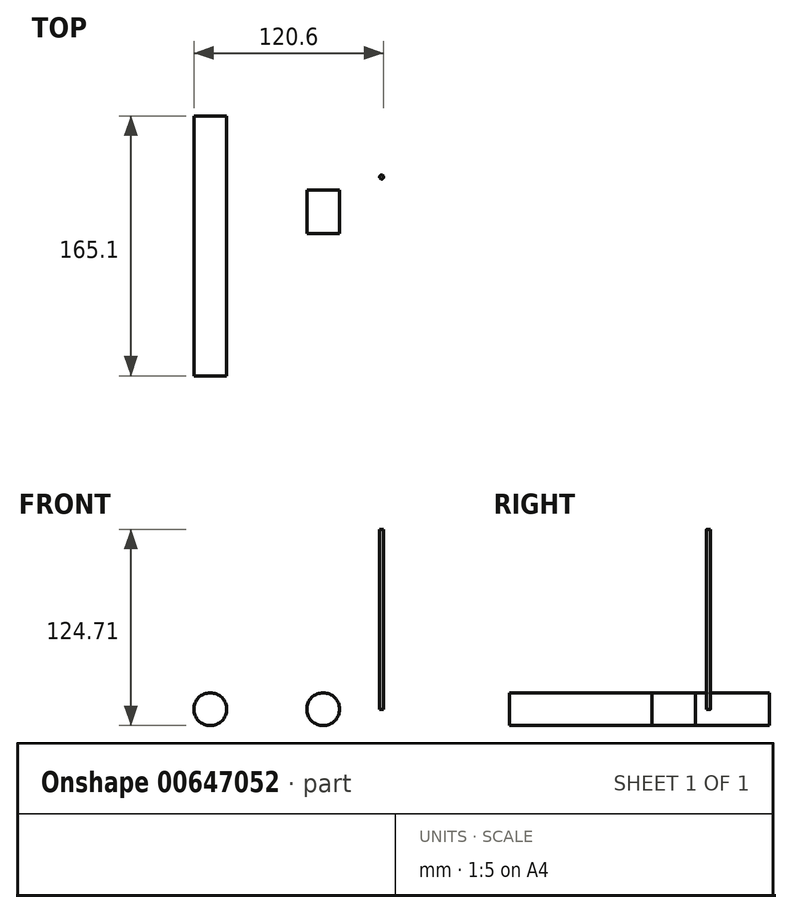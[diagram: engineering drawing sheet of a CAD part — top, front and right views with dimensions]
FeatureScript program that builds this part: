
annotation { "Feature Type Name" : "Feature", "Feature Type Description" : "" }
export const myFeature = defineFeature(function(context is Context, id is Id, definition is map)
    precondition{}
    {
        {
            var Q0;
            Q0=qCreatedBy(makeId("Top.planeOp"),FACE);
            var sketch = newSketch(context, id + "F0", { "sketchPlane" : qUnion([Q0])});
            skLineSegment(sketch, "E0.bottom", {"start": v(0, 0) * mm, "end": v(10.41, 0) * mm});
            skLineSegment(sketch, "E0.top", {"start": v(0, 27.62) * mm, "end": v(10.41, 27.62) * mm});
            skLineSegment(sketch, "E0.left", {"start": v(0, 0) * mm, "end": v(0, 27.62) * mm});
            skLineSegment(sketch, "E0.right", {"start": v(10.41, 0) * mm, "end": v(10.41, 27.62) * mm});
            skLineSegment(sketch, "E1.bottom", {"start": v(0, 27.62) * mm, "end": v(6.35, 27.62) * mm});
            skLineSegment(sketch, "E1.top", {"start": v(0, 0) * mm, "end": v(6.35, 0) * mm});
            skLineSegment(sketch, "E1.left", {"start": v(0, 27.62) * mm, "end": v(0, 0) * mm});
            skLineSegment(sketch, "E1.right", {"start": v(6.35, 27.62) * mm, "end": v(6.35, 0) * mm});
            skSolve(sketch);
        }
        {
            var Q0;
            Q0=makeQuery(id+"F0.imprint","IMPRINT",FACE,{"disambiguationData":[TD([[makeQuery(id+"F0.imprint","IMPRINT",EDGE,{"derivedFrom":sQuery(id+"F0.wireOp",EDGE,"E0.bottom")}),1.0]])]});
            var Q1;
            Q1=sQuery(id+"F0.wireOp",EDGE,"E1.left");
            revolve(context, id + "F1", {"entities" : qUnion([Q0]), "axis" : qUnion([Q1]), "revolveType" : RevolveType.FULL});
        }
        {
            var Q0;
            Q0=qCreatedBy(makeId("Top.planeOp"),FACE);
            var sketch = newSketch(context, id + "F2", { "sketchPlane" : qUnion([Q0])});
            skLineSegment(sketch, "E2.bottom", {"start": v(-82.15, 74.6) * mm, "end": v(-71.73, 74.6) * mm});
            skLineSegment(sketch, "E2.top", {"start": v(-82.15, -90.5) * mm, "end": v(-71.73, -90.5) * mm});
            skLineSegment(sketch, "E2.left", {"start": v(-82.15, 74.6) * mm, "end": v(-82.15, -90.5) * mm});
            skLineSegment(sketch, "E2.right", {"start": v(-71.73, 74.6) * mm, "end": v(-71.73, -90.5) * mm});
            skLineSegment(sketch, "E3.bottom", {"start": v(-71.73, 74.6) * mm, "end": v(-78.08, 74.6) * mm});
            skLineSegment(sketch, "E3.top", {"start": v(-71.73, -90.5) * mm, "end": v(-78.08, -90.5) * mm});
            skLineSegment(sketch, "E3.right", {"start": v(-78.08, 74.6) * mm, "end": v(-78.08, -90.5) * mm});
            skSolve(sketch);
        }
        {
            var Q0;
            Q0=makeQuery(id+"F2.imprint","IMPRINT",FACE,{"disambiguationData":[TD([[makeQuery(id+"F2.imprint","IMPRINT",EDGE,{"derivedFrom":sQuery(id+"F2.wireOp",EDGE,"E2.bottom")}),-1.0]])]});
            var Q1;
            Q1=sQuery(id+"F2.wireOp",EDGE,"E2.right");
            revolve(context, id + "F3", {"entities" : qUnion([Q0]), "axis" : qUnion([Q1]), "revolveType" : RevolveType.FULL});
        }
        {
            var Q0;
            Q0=qCreatedBy(makeId("Top.planeOp"),FACE);
            var sketch = newSketch(context, id + "F4", { "sketchPlane" : qUnion([Q0])});
            skCircle(sketch, "E4", {"center": v(37.18, 35.78) * mm, "radius": 1.27 * mm});
            skSolve(sketch);
        }
        {
            var Q0;
            Q0=makeQuery(id+"F4.imprint","IMPRINT",FACE,{"disambiguationData":[TD([[makeQuery(id+"F4.imprint","IMPRINT",EDGE,{"derivedFrom":sQuery(id+"F4.wireOp",EDGE,"E4")}),1.0]])]});
            extrude(context, id + "F5", {"entities" : qUnion([Q0]), "depth" : 114.3 * mm, "offsetDistance" : 25.4 * mm});
        }
    });
